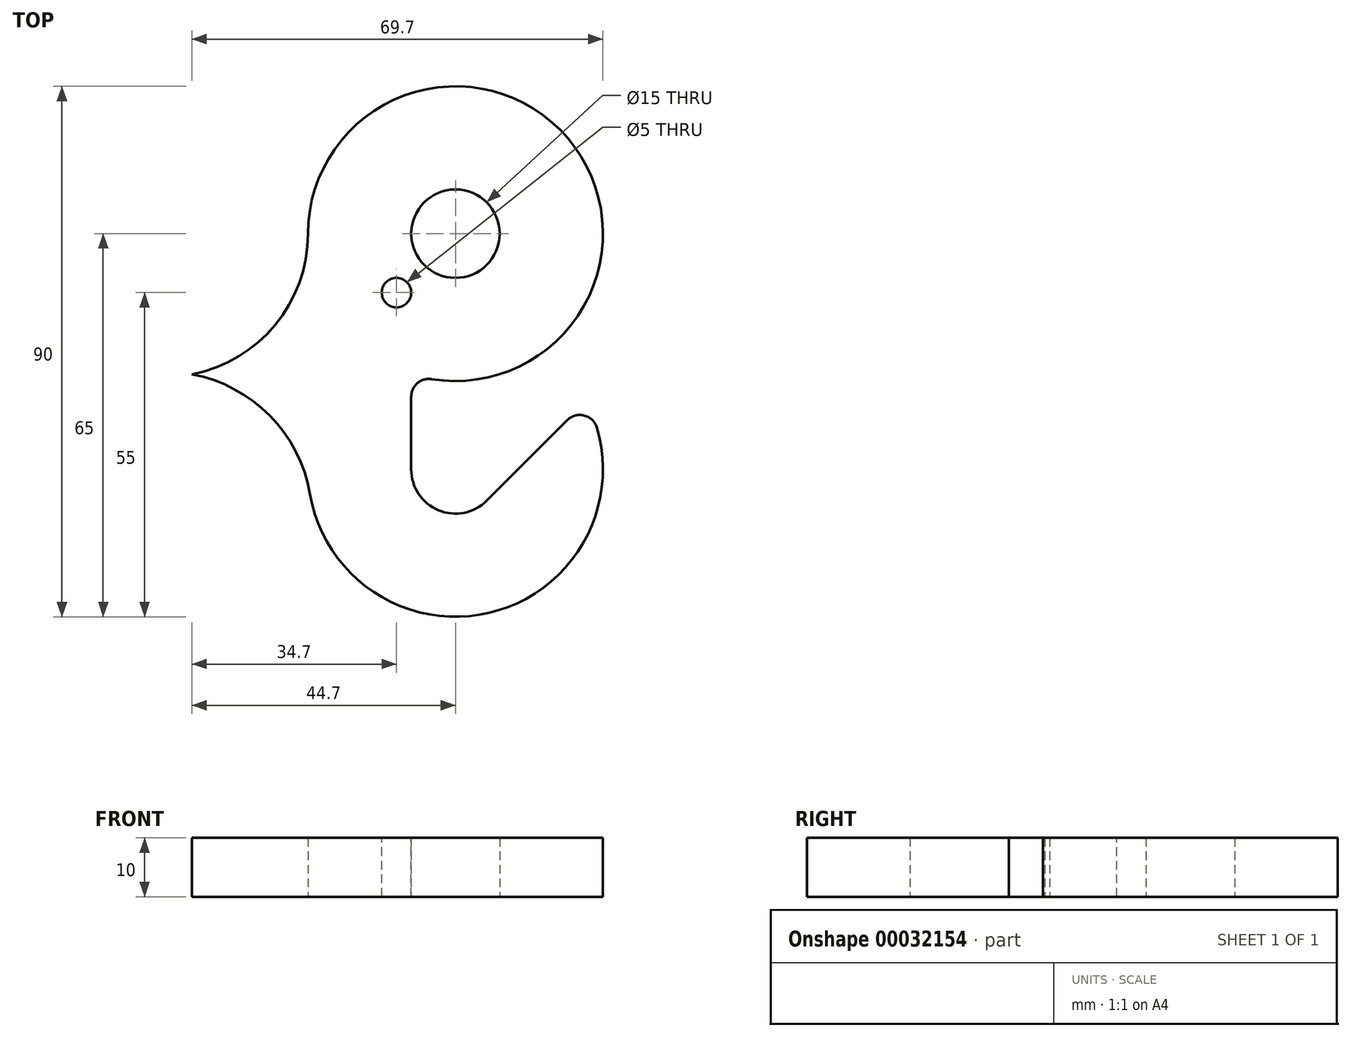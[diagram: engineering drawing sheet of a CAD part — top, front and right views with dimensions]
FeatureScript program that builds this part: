
annotation { "Feature Type Name" : "Feature", "Feature Type Description" : "" }
export const myFeature = defineFeature(function(context is Context, id is Id, definition is map)
    precondition{}
    {
        {
            var Q0;
            Q0=qCreatedBy(makeId("Top.planeOp"),FACE);
            var sketch = newSketch(context, id + "F0", { "sketchPlane" : qUnion([Q0])});
            skCircle(sketch, "E0", {"center": v(0, 0) * mm, "radius": 7.5 * mm});
            skArc(sketch, "E1", {"start": v(-7.5, -23.85) * mm, "mid": v(20.16, 14.8) * mm, "end": v(-25, 0) * mm});
            skArc(sketch, "E2", {"start": v(-24.64, -44.21) * mm, "mid": v(7.98, -63.7) * mm, "end": v(22.17, -28.44) * mm});
            skArc(sketch, "E3", {"start": v(-7.5, -40) * mm, "mid": v(-2.87, -46.93) * mm, "end": v(5.3, -45.3) * mm});
            skLineSegment(sketch, "E4", {"start": v(22.17, -28.44) * mm, "end": v(5.3, -45.3) * mm});
            skLineSegment(sketch, "E5", {"start": v(-7.5, -23.85) * mm, "end": v(-7.5, -40) * mm});
            skPoint(sketch, "E6", {"position": v(-10, -10) * mm});
            skArc(sketch, "E7", {"start": v(-44.7, -23.85) * mm, "mid": v(-30.56, -15.47) * mm, "end": v(-25, 0) * mm});
            skArc(sketch, "E8", {"start": v(-24.64, -44.21) * mm, "mid": v(-31.47, -30.88) * mm, "end": v(-44.7, -23.85) * mm});
            skSolve(sketch);
        }
        {
            var Q0;
            Q0 = qSketchRegion(id + "F0", true);
            extrude(context, id + "F1", {"entities" : qUnion([Q0]), "endBound" : BoundingType.SYMMETRIC, "depth" : 10 * mm});
        }
        {
            var Q0;
            Q0=makeQuery(id+"F1.opExtrude","SWEPT_EDGE",EDGE,{"disambiguationData":[OSD([sQuery(id+"F0.wireOp",EDGE,"E2"),sQuery(id+"F0.wireOp",EDGE,"E4")])]});
            var Q1;
            Q1=makeQuery(id+"F1.opExtrude","SWEPT_EDGE",EDGE,{"disambiguationData":[OSD([sQuery(id+"F0.wireOp",EDGE,"E1"),sQuery(id+"F0.wireOp",EDGE,"E5")])]});
            fillet(context, id + "F2", {"entities" : qUnion([Q0, Q1]), "radius" : 3 * mm, "tangentPropagation" : true, "allowEdgeOverflow" : false});
        }
        {
            var Q0;
            Q0=qCreatedBy(makeId("Top.planeOp"),FACE);
            var sketch = newSketch(context, id + "F3", { "sketchPlane" : qUnion([Q0])});
            skCircle(sketch, "E9", {"center": v(-10, -10) * mm, "radius": 3.5 * mm});
            skSolve(sketch);
        }
        {
            var Q0;
            Q0=makeQuery(id+"F1.opExtrude","CAP_FACE",FACE,{"disambiguationData":[OSD([sQuery(id+"F0.wireOp",EDGE,"E0"),sQuery(id+"F0.wireOp",EDGE,"E1"),sQuery(id+"F0.wireOp",EDGE,"E2"),sQuery(id+"F0.wireOp",EDGE,"11476423-ecff-455c-9466-ff6b3bc0928e"),sQuery(id+"F0.wireOp",EDGE,"E3"),sQuery(id+"F0.wireOp",EDGE,"E4"),sQuery(id+"F0.wireOp",EDGE,"E5")])],"isStart":false});
            var sketch = newSketch(context, id + "F4", { "sketchPlane" : qUnion([Q0])});
            skCircle(sketch, "E10.0", {"center": v(-10, -10) * mm, "radius": 3.5 * mm});
            skSolve(sketch);
        }
        {
            var Q0;
            Q0=sQuery(id+"F4.wireOp",VERTEX,"E10.0.center");
            var Q1;
            Q1=makeQuery(id+"F1.opExtrude","SWEPT_BODY",BODY,{"disambiguationData":[OSD([sQuery(id+"F0.wireOp",EDGE,"E0"),sQuery(id+"F0.wireOp",EDGE,"E1"),sQuery(id+"F0.wireOp",EDGE,"E2"),sQuery(id+"F0.wireOp",EDGE,"11476423-ecff-455c-9466-ff6b3bc0928e"),sQuery(id+"F0.wireOp",EDGE,"E3"),sQuery(id+"F0.wireOp",EDGE,"E4"),sQuery(id+"F0.wireOp",EDGE,"E5")])]});
            hole(context, id + "F5", {"style" : HoleStyle.SIMPLE, "holeDiameter" : 5 * mm, "endStyle" : HoleEndStyle.THROUGH, "locations" : qUnion([Q0]), "scope" : qUnion([Q1])});
        }
    });
